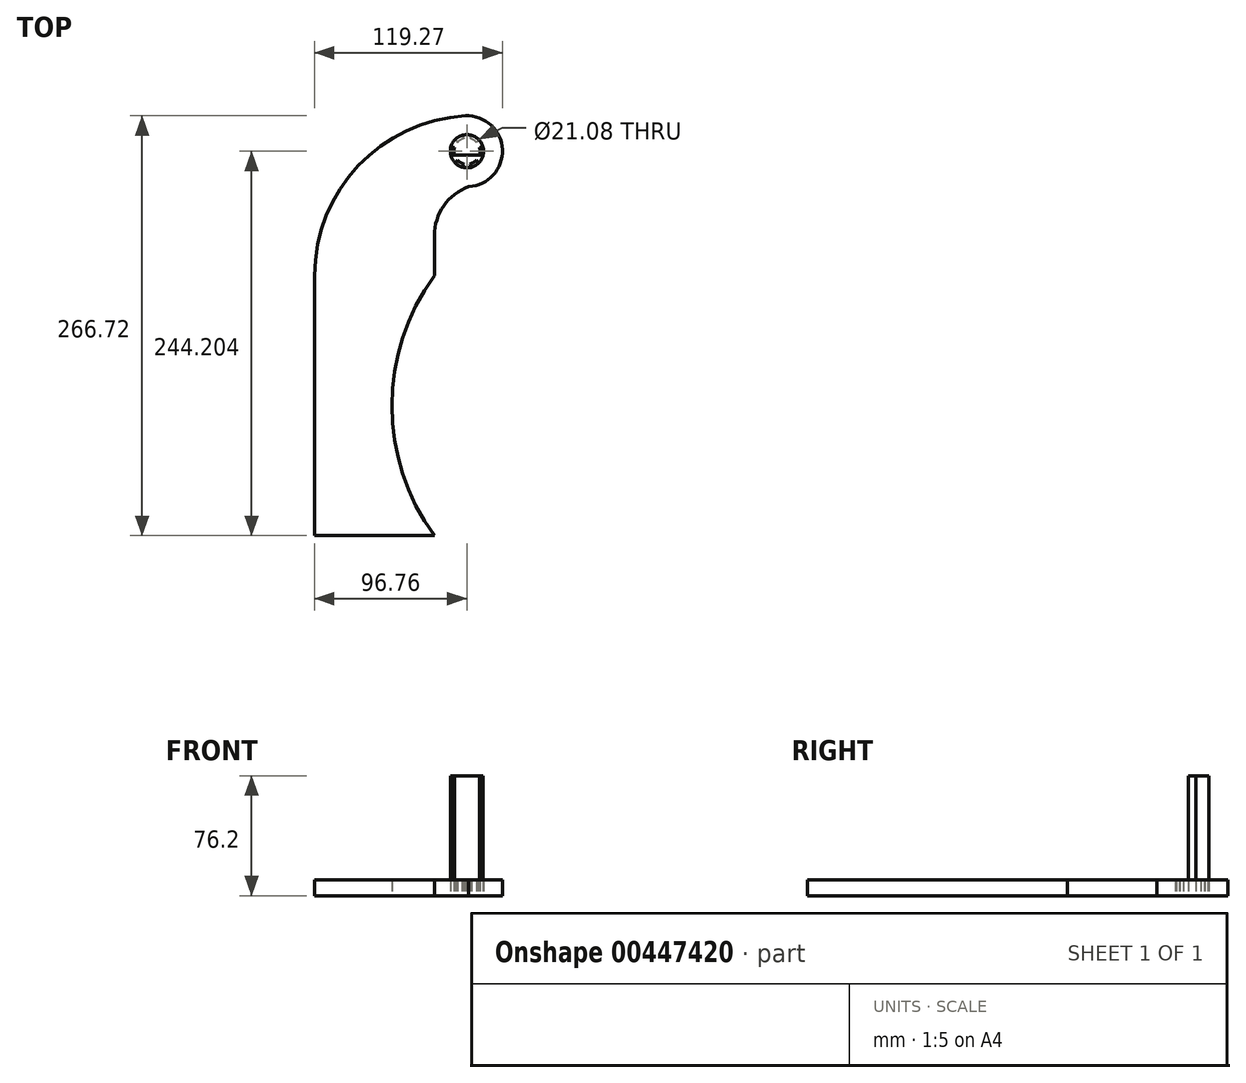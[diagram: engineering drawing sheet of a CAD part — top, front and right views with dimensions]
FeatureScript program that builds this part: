
annotation { "Feature Type Name" : "Feature", "Feature Type Description" : "" }
export const myFeature = defineFeature(function(context is Context, id is Id, definition is map)
    precondition{}
    {
        {
            var Q0;
            Q0=qCreatedBy(makeId("Top.planeOp"),FACE);
            var sketch = newSketch(context, id + "F0", { "sketchPlane" : qUnion([Q0])});
            skLineSegment(sketch, "E0.bottom", {"start": v(-112.7, -82.55) * mm, "end": v(-188.75, -82.55) * mm});
            skLineSegment(sketch, "E0.top", {"start": v(-112.7, 82.55) * mm, "end": v(-188.75, 82.55) * mm});
            skLineSegment(sketch, "E0.right", {"start": v(-188.75, -82.55) * mm, "end": v(-188.75, 82.55) * mm});
            skArc(sketch, "E1", {"start": v(-112.7, 82.55) * mm, "mid": v(-139.68, 0) * mm, "end": v(-112.7, -82.55) * mm});
            skLineSegment(sketch, "E2", {"start": v(-112.7, 82.55) * mm, "end": v(-112.7, 107.95) * mm});
            skLineSegment(sketch, "E3", {"start": v(-90.86, 139.17) * mm, "end": v(-92.87, 184.15) * mm});
            skArc(sketch, "E4", {"start": v(-90.86, 139.17) * mm, "mid": v(-106.7, 127) * mm, "end": v(-112.7, 107.95) * mm});
            skArc(sketch, "E5", {"start": v(-92.87, 184.15) * mm, "mid": v(-161, 152.4) * mm, "end": v(-188.75, 82.55) * mm});
            skArc(sketch, "E6", {"start": v(-90.86, 139.17) * mm, "mid": v(-69.5, 162.66) * mm, "end": v(-92.87, 184.15) * mm});
            skLineSegment(sketch, "E7", {"start": v(0, 0) * mm, "end": v(0, 187.7) * mm});
            skCircle(sketch, "E8", {"center": v(-92, 161.65) * mm, "radius": 10.54 * mm});
            skCircle(sketch, "E9", {"center": v(-92, 161.65) * mm, "radius": 8.26 * mm});
            skLineSegment(sketch, "E10.bottom", {"start": v(-81.73, 164.07) * mm, "end": v(-102.25, 164.07) * mm});
            skLineSegment(sketch, "E10.top", {"start": v(-81.73, 159.24) * mm, "end": v(-102.25, 159.24) * mm});
            skSolve(sketch);
        }
        {
            var Q0;
            Q0=makeQuery(id+"F0.imprint","IMPRINT",FACE,{"disambiguationData":[TD([[makeQuery(id+"F0.imprint","IMPRINT",EDGE,{"derivedFrom":sQuery(id+"F0.wireOp",EDGE,"E0.bottom")}),-1.0]])]});
            var Q1;
            Q1=makeQuery(id+"F0.imprint","IMPRINT",FACE,{"disambiguationData":[TD([[makeQuery(id+"F0.imprint","IMPRINT",EDGE,{"derivedFrom":sQuery(id+"F0.wireOp",EDGE,"E0.top")}),-1.0]])]});
            var Q2;
            {var subQ0=sQuery(id+"F0.wireOp",EDGE,"E6");Q2=makeQuery(id+"F0.imprint","IMPRINT",FACE,{"disambiguationData":[TD([[makeQuery(id+"F0.imprint","IMPRINT",EDGE,{"derivedFrom":subQ0}),1.0]])]});}
            extrude(context, id + "F1", {"entities" : qUnion([Q0, Q1, Q2]), "depth" : 10.16 * mm});
        }
        {
            var Q0;
            {var subQ0=sQuery(id+"F0.wireOp",EDGE,"E9");var subQ1=sQuery(id+"F0.wireOp",EDGE,"E3");var subQ2=makeQuery(id+"F0.imprint","INTERSECT",VERTEX,{"disambiguationData":[OD(0.0)],"derivedFrom":[subQ1,subQ0]});Q0=makeQuery(id+"F0.imprint","IMPRINT",FACE,{"disambiguationData":[TD([[makeQuery(id+"F0.imprint","IMPRINT",EDGE,{"disambiguationData":[TD([[subQ2,-1.0]])],"derivedFrom":subQ1}),-1.0]])]});}
            var Q1;
            {var subQ0=sQuery(id+"F0.wireOp",EDGE,"E9");var subQ1=sQuery(id+"F0.wireOp",EDGE,"E3");var subQ2=makeQuery(id+"F0.imprint","INTERSECT",VERTEX,{"disambiguationData":[OD(0.0)],"derivedFrom":[subQ1,subQ0]});Q1=makeQuery(id+"F0.imprint","IMPRINT",FACE,{"disambiguationData":[TD([[makeQuery(id+"F0.imprint","IMPRINT",EDGE,{"disambiguationData":[TD([[subQ2,-1.0]])],"derivedFrom":subQ1}),1.0]])]});}
            var Q2;
            {var subQ0=sQuery(id+"F0.wireOp",EDGE,"E10.top");var subQ1=sQuery(id+"F0.wireOp",EDGE,"E3");var subQ2=makeQuery(id+"F0.imprint","INTERSECT",VERTEX,{"derivedFrom":[subQ1,subQ0]});Q2=makeQuery(id+"F0.imprint","IMPRINT",FACE,{"disambiguationData":[TD([[makeQuery(id+"F0.imprint","IMPRINT",EDGE,{"disambiguationData":[TD([[subQ2,-1.0]])],"derivedFrom":subQ1}),1.0]])]});}
            var Q3;
            {var subQ0=sQuery(id+"F0.wireOp",EDGE,"E10.bottom");var subQ1=sQuery(id+"F0.wireOp",EDGE,"E3");var subQ2=makeQuery(id+"F0.imprint","INTERSECT",VERTEX,{"derivedFrom":[subQ1,subQ0]});Q3=makeQuery(id+"F0.imprint","IMPRINT",FACE,{"disambiguationData":[TD([[makeQuery(id+"F0.imprint","IMPRINT",EDGE,{"disambiguationData":[TD([[subQ2,-1.0]])],"derivedFrom":subQ1}),1.0]])]});}
            var Q4;
            {var subQ0=sQuery(id+"F0.wireOp",EDGE,"E10.bottom");var subQ1=sQuery(id+"F0.wireOp",EDGE,"E3");var subQ2=makeQuery(id+"F0.imprint","INTERSECT",VERTEX,{"derivedFrom":[subQ1,subQ0]});Q4=makeQuery(id+"F0.imprint","IMPRINT",FACE,{"disambiguationData":[TD([[makeQuery(id+"F0.imprint","IMPRINT",EDGE,{"disambiguationData":[TD([[subQ2,-1.0]])],"derivedFrom":subQ1}),-1.0]])]});}
            var Q5;
            {var subQ0=sQuery(id+"F0.wireOp",EDGE,"E10.top");var subQ1=sQuery(id+"F0.wireOp",EDGE,"E3");var subQ2=makeQuery(id+"F0.imprint","INTERSECT",VERTEX,{"derivedFrom":[subQ1,subQ0]});Q5=makeQuery(id+"F0.imprint","IMPRINT",FACE,{"disambiguationData":[TD([[makeQuery(id+"F0.imprint","IMPRINT",EDGE,{"disambiguationData":[TD([[subQ2,-1.0]])],"derivedFrom":subQ1}),-1.0]])]});}
            extrude(context, id + "F2", {"entities" : qUnion([Q0, Q1, Q2, Q3, Q4, Q5]), "depth" : 76.2 * mm});
        }
        {
            var Q0;
            {var subQ0=sQuery(id+"F0.wireOp",EDGE,"E10.bottom");var subQ1=sQuery(id+"F0.wireOp",EDGE,"E8");var subQ2=makeQuery(id+"F0.imprint","INTERSECT",VERTEX,{"disambiguationData":[OD(0.0)],"derivedFrom":[subQ1,subQ0]});Q0=makeQuery(id+"F0.imprint","IMPRINT",FACE,{"disambiguationData":[TD([[makeQuery(id+"F0.imprint","IMPRINT",EDGE,{"disambiguationData":[TD([[subQ2,1.0]])],"derivedFrom":subQ1}),1.0]])]});}
            extrude(context, id + "F3", {"entities" : qUnion([Q0]), "depth" : 10.16 * mm});
        }
        {
            var Q0;
            Q0=makeQuery(id+"F3.opExtrude","SWEPT_BODY",BODY,{"disambiguationData":[OSD([sQuery(id+"F0.wireOp",EDGE,"E8"),sQuery(id+"F0.wireOp",EDGE,"E9"),sQuery(id+"F0.wireOp",EDGE,"E10.bottom"),sQuery(id+"F0.wireOp",EDGE,"E10.top")])]});
            var Q1;
            Q1=sQuery(id+"F0.wireOp",EDGE,"E9");
            circularPattern(context, id + "F4", {"entities" : qUnion([Q0]), "axis" : qUnion([Q1]), "angle" : 360 * degree, "instanceCount" : 6, "equalSpace" : true});
        }
    });
